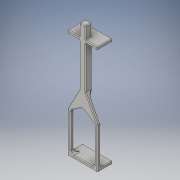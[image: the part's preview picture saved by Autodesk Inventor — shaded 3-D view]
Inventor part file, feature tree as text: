
AUTODESK INVENTOR PART (.ipt)
format: ipt  version: 2016 (Build 200138000, 138)  size: 365,568 bytes
history: native  units: mm
features: extrude x5, sketch x5, fillet x4, projected_geometry x4
ambient origin geometry x8: Origin, YZ Plane, XZ Plane, XY Plane, X Axis, Y Axis, Z Axis, Center Point
bodies: Solid1 (feature_tree)
feature tree (18):
  extrude  "Extrusion1"  Depth=19.8mm
  extrude  "Extrusion2"  Depth=2.0mm
  extrude  "Extrusion3"  Depth=2.0mm
  extrude  "Extrusion4"  Depth=25.0mm TaperAngle=0.0deg
  extrude  "Extrusion5"  Depth=4.0mm
  fillet  "Fillet1"  Radius=15.0mm
  fillet  "Fillet2"  Radius=15.0mm
  fillet  "Fillet3"  Radius=80.0mm
  fillet  "Fillet4"  Radius=15.0mm
  sketch  "Sketch1"  dims[d0=9.8mm d1=19.8mm]
  sketch  "Sketch2"  dims[d2=2.0mm d3=0.0mm d4=2.0mm]
  projected_geometry  "Projected Loop1"
  sketch  "Sketch4"  dims[d5=2.0mm d6=2.0mm]
  projected_geometry  "Projected Loop3"
  sketch  "Sketch6"  dims[d7=2.0mm d8=25.0mm d9=0.0mm]
  projected_geometry  "Projected Loop4"
  sketch  "Sketch7"  dims[d15=5.0mm d16=4.0mm d17=15.0mm d18=15.0mm d19=80.0mm d20=15.0mm d21=0.0mm d22=2.0mm d23=7.0mm d24=38.0mm d25=4.0mm d26=0.0mm d27=70.0mm d28=2.0mm d29=19.8mm d30=4.0mm d31=0.0mm d32=2.0mm d33=0.5mm d34=0.5mm d35=0.5mm]
  projected_geometry  "Projected Loop5"
